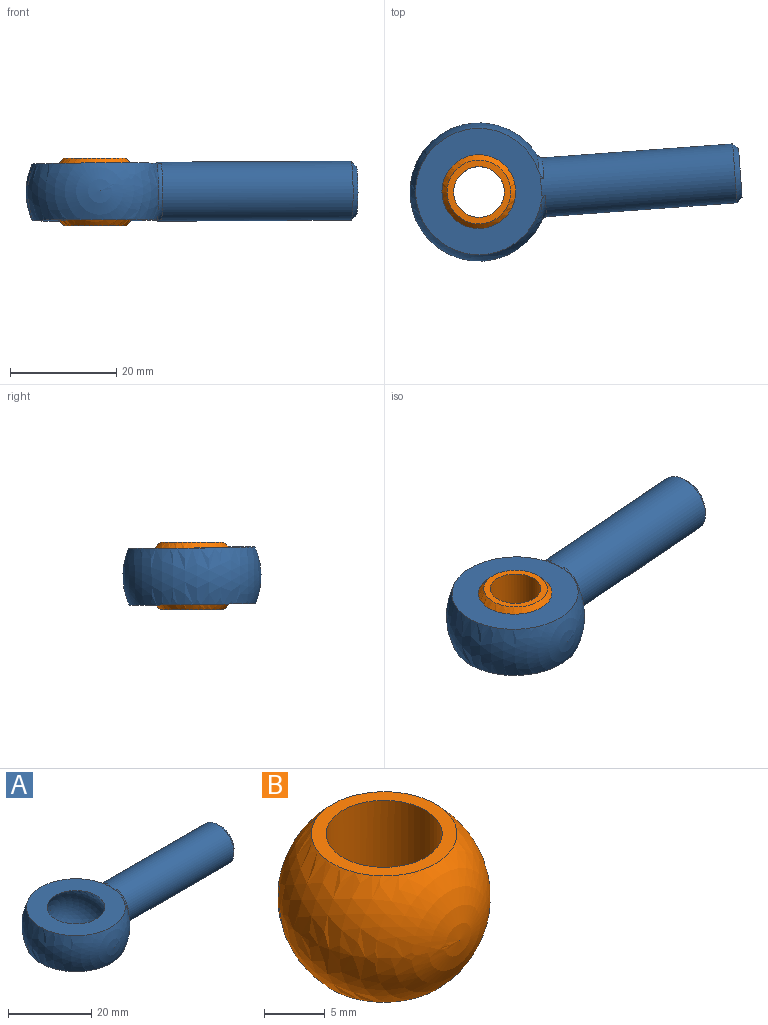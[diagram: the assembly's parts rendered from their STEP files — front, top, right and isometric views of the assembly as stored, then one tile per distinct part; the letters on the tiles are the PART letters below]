
ASSEMBLY  parts=2 mates=1
PART A: 11 faces, bbox 62.2x26x26 mm
  f0: sphere r=13mm, area 749.6mm2, adj f1,f3,f8,f9
  f1: plane 24.24x23.74mm, normal (0,0,1), area 291.9mm2, adj f0,f2,f4,f6,f8,f9
  f2: sphere r=8.73mm, area 581.4mm2, adj f1,f3
  f3: plane 24.24x23.74mm, normal (0,0,-1), area 291.9mm2, adj f0,f2,f5,f6,f8,f9
  f4: sphere r=13mm, area 0.6mm2, adj f1,f6
  f5: sphere r=13mm, area 0.6mm2, adj f3,f6
  f6: cylinder r=5.55mm len=36.47mm, axis (1,0,0), area 1254.5mm2, adj f1,f3,f4,f5,f8,f9,f10
  f7: plane 9.1x9.1mm, normal (1,0,0), area 65mm2, adj f10
  f8: torus R=6.55mm, axis (-1,0,0), area 14.7mm2, adj f0,f1,f3,f6
  f9: torus R=6.55mm, axis (-1,0,0), area 14.7mm2, adj f0,f1,f3,f6
  f10: cone r=4.55mm half-angle=45deg, axis (-1,0,0), area 44.9mm2, adj f6,f7
PART B: 4 faces, bbox 17.5x17.5x17.5 mm
  f0: sphere r=8.72mm, area 696.3mm2, adj f2,f3
  f1: cylinder r=4.77mm len=12.7mm, axis (0,0,1), area 380.2mm2, adj f2,f3
  f2: plane 11.97x11.97mm, normal (0,0,1), area 41.1mm2, adj f0,f1
  f3: plane 11.97x11.97mm, normal (0,0,-1), area 41.1mm2, adj f0,f1
PLACE A rot(axis=(-0.2,-0.08,0.98),4.3deg) t=(-1.81,5.19,-1.42)mm
PLACE B t=(-1.81,5.19,-1.42)mm fixed
MATE ball A.f2 <-> B.f1  axis (-0.01,0.01,1) through (-1.81,5.19,-1.42)mm
